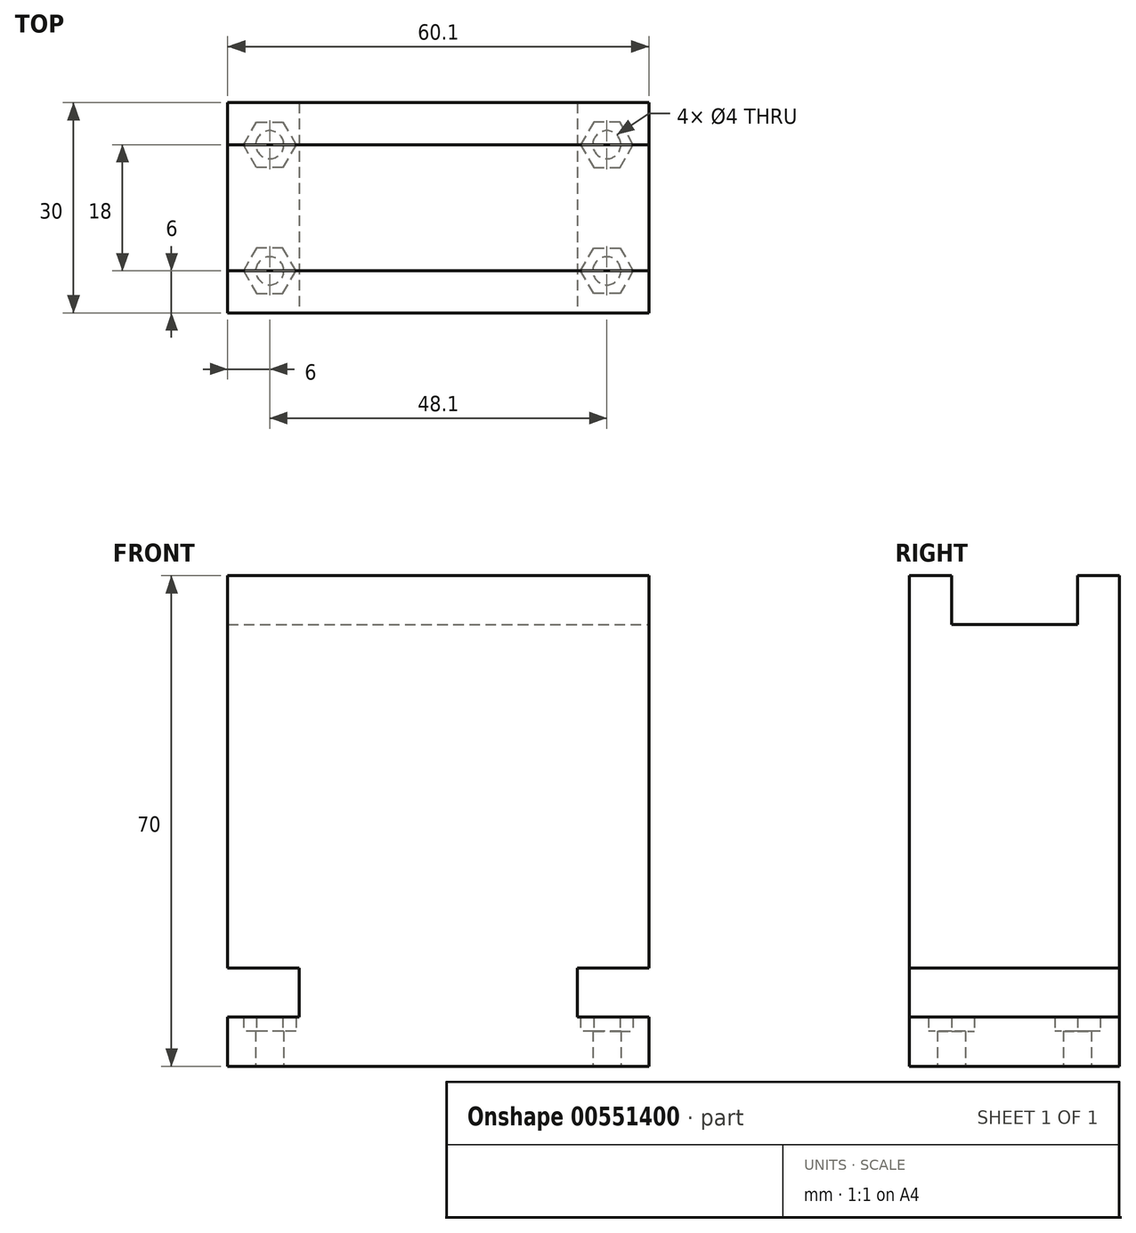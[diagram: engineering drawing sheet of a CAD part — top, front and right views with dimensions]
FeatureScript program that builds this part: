
annotation { "Feature Type Name" : "Feature", "Feature Type Description" : "" }
export const myFeature = defineFeature(function(context is Context, id is Id, definition is map)
    precondition{}
    {
        {
            var Q0;
            Q0=qCreatedBy(makeId("Top.planeOp"),FACE);
            var sketch = newSketch(context, id + "F0", { "sketchPlane" : qUnion([Q0])});
            skLineSegment(sketch, "E0.bottom", {"start": v(-30.05, 15) * mm, "end": v(30.05, 15) * mm});
            skLineSegment(sketch, "E0.top", {"start": v(-30.05, -15) * mm, "end": v(30.05, -15) * mm});
            skLineSegment(sketch, "E0.left", {"start": v(-30.05, 15) * mm, "end": v(-30.05, -15) * mm});
            skLineSegment(sketch, "E0.right", {"start": v(30.05, 15) * mm, "end": v(30.05, -15) * mm});
            skCircle(sketch, "E1", {"center": v(-24.05, 9) * mm, "radius": 2 * mm});
            skCircle(sketch, "E2.MirrorC", {"center": v(24.05, 9) * mm, "radius": 2 * mm});
            skCircle(sketch, "E3.MirrorC", {"center": v(-24.05, -9) * mm, "radius": 2 * mm});
            skCircle(sketch, "E4.MirrorC", {"center": v(24.05, -9) * mm, "radius": 2 * mm});
            skSolve(sketch);
        }
        {
            var Q0;
            Q0 = qSketchRegion(id + "F0", true);
            extrude(context, id + "F1", {"entities" : qUnion([Q0]), "depth" : 5 * mm, "offsetDistance" : 25 * mm});
        }
        {
            var Q0;
            Q0=makeQuery(id+"F1.opExtrude","CAP_FACE",FACE,{"disambiguationData":[OSD([sQuery(id+"F0.wireOp",EDGE,"E0.bottom"),sQuery(id+"F0.wireOp",EDGE,"E0.top"),sQuery(id+"F0.wireOp",EDGE,"E0.left"),sQuery(id+"F0.wireOp",EDGE,"E0.right"),sQuery(id+"F0.wireOp",EDGE,"E1"),sQuery(id+"F0.wireOp",EDGE,"E2.MirrorC"),sQuery(id+"F0.wireOp",EDGE,"E3.MirrorC"),sQuery(id+"F0.wireOp",EDGE,"E4.MirrorC")])],"isStart":false});
            var sketch = newSketch(context, id + "F2", { "sketchPlane" : qUnion([Q0])});
            skCircle(sketch, "E5.cCircle", {"center": v(-24.05, 9) * mm, "radius": 3.25 * mm, "construction": true});
            skLineSegment(sketch, "E5.0", {"start": v(-25.93, 5.75) * mm, "end": v(-27.8, 9) * mm});
            skLineSegment(sketch, "E5.1", {"start": v(-27.8, 9) * mm, "end": v(-25.93, 12.25) * mm});
            skLineSegment(sketch, "E5.2", {"start": v(-25.93, 12.25) * mm, "end": v(-22.17, 12.25) * mm});
            skLineSegment(sketch, "E5.3", {"start": v(-22.17, 12.25) * mm, "end": v(-20.3, 9) * mm});
            skLineSegment(sketch, "E5.4", {"start": v(-20.3, 9) * mm, "end": v(-22.17, 5.75) * mm});
            skLineSegment(sketch, "E5.5", {"start": v(-22.17, 5.75) * mm, "end": v(-25.93, 5.75) * mm});
            skPoint(sketch, "E5.0.midPoint", {"position": v(-26.86, 7.37) * mm});
            skLineSegment(sketch, "E6.MirrorCS", {"start": v(22.17, 5.75) * mm, "end": v(25.93, 5.75) * mm});
            skLineSegment(sketch, "E7.MirrorCS", {"start": v(27.8, 9) * mm, "end": v(25.93, 12.25) * mm});
            skLineSegment(sketch, "E8.MirrorCS", {"start": v(20.3, 9) * mm, "end": v(22.17, 5.75) * mm});
            skLineSegment(sketch, "E9.MirrorCS", {"start": v(22.17, 12.25) * mm, "end": v(20.3, 9) * mm});
            skLineSegment(sketch, "E10.MirrorCS", {"start": v(25.93, 12.25) * mm, "end": v(22.17, 12.25) * mm});
            skLineSegment(sketch, "E11.MirrorCS", {"start": v(25.93, 5.75) * mm, "end": v(27.8, 9) * mm});
            skCircle(sketch, "E12.MirrorC", {"center": v(24.05, 9) * mm, "radius": 3.25 * mm, "construction": true});
            skPoint(sketch, "E13.MirrorP", {"position": v(26.86, 7.37) * mm});
            skLineSegment(sketch, "E14.MirrorCS", {"start": v(22.17, -5.75) * mm, "end": v(25.93, -5.75) * mm});
            skLineSegment(sketch, "E15.MirrorCS", {"start": v(25.93, -5.75) * mm, "end": v(27.8, -9) * mm});
            skLineSegment(sketch, "E16.MirrorCS", {"start": v(27.8, -9) * mm, "end": v(25.93, -12.25) * mm});
            skLineSegment(sketch, "E17.MirrorCS", {"start": v(20.3, -9) * mm, "end": v(22.17, -5.75) * mm});
            skLineSegment(sketch, "E18.MirrorCS", {"start": v(25.93, -12.25) * mm, "end": v(22.17, -12.25) * mm});
            skLineSegment(sketch, "E19.MirrorCS", {"start": v(22.17, -12.25) * mm, "end": v(20.3, -9) * mm});
            skPoint(sketch, "E20.MirrorP", {"position": v(26.86, -7.37) * mm});
            skCircle(sketch, "E21.MirrorC", {"center": v(24.05, -9) * mm, "radius": 3.25 * mm, "construction": true});
            skLineSegment(sketch, "E22.MirrorCS", {"start": v(-22.17, -5.75) * mm, "end": v(-25.93, -5.75) * mm});
            skLineSegment(sketch, "E23.MirrorCS", {"start": v(-20.3, -9) * mm, "end": v(-22.17, -5.75) * mm});
            skLineSegment(sketch, "E24.MirrorCS", {"start": v(-22.17, -12.25) * mm, "end": v(-20.3, -9) * mm});
            skLineSegment(sketch, "E25.MirrorCS", {"start": v(-25.93, -12.25) * mm, "end": v(-22.17, -12.25) * mm});
            skPoint(sketch, "E26.MirrorP", {"position": v(-26.86, -7.37) * mm});
            skLineSegment(sketch, "E27.MirrorCS", {"start": v(-27.8, -9) * mm, "end": v(-25.93, -12.25) * mm});
            skLineSegment(sketch, "E28.MirrorCS", {"start": v(-25.93, -5.75) * mm, "end": v(-27.8, -9) * mm});
            skCircle(sketch, "E29.MirrorC", {"center": v(-24.05, -9) * mm, "radius": 3.25 * mm, "construction": true});
            skSolve(sketch);
        }
        {
            var Q0;
            Q0=makeQuery(id+"F2.imprint","IMPRINT",FACE,{"disambiguationData":[TD([[makeQuery(id+"F2.imprint","IMPRINT",EDGE,{"derivedFrom":sQuery(id+"F2.wireOp",EDGE,"E5.0")}),1.0]])]});
            extrude(context, id + "F3", {"entities" : qUnion([Q0]), "operationType" : NewBodyOperationType.ADD, "depth" : 2 * mm, "offsetDistance" : 25 * mm});
        }
        {
            var Q0;
            Q0=makeQuery(id+"F3.opExtrude","CAP_FACE",FACE,{"disambiguationData":[OSD([sQuery(id+"F0.wireOp",EDGE,"E0.bottom"),sQuery(id+"F0.wireOp",EDGE,"E0.top"),sQuery(id+"F0.wireOp",EDGE,"E0.left"),sQuery(id+"F0.wireOp",EDGE,"E0.right"),sQuery(id+"F2.wireOp",EDGE,"E5.0"),sQuery(id+"F2.wireOp",EDGE,"E5.1"),sQuery(id+"F2.wireOp",EDGE,"E5.2"),sQuery(id+"F2.wireOp",EDGE,"E5.3"),sQuery(id+"F2.wireOp",EDGE,"E5.4"),sQuery(id+"F2.wireOp",EDGE,"E5.5"),sQuery(id+"F2.wireOp",EDGE,"E6.MirrorCS"),sQuery(id+"F2.wireOp",EDGE,"E7.MirrorCS"),sQuery(id+"F2.wireOp",EDGE,"E8.MirrorCS"),sQuery(id+"F2.wireOp",EDGE,"E9.MirrorCS"),sQuery(id+"F2.wireOp",EDGE,"E10.MirrorCS"),sQuery(id+"F2.wireOp",EDGE,"E11.MirrorCS"),sQuery(id+"F2.wireOp",EDGE,"E14.MirrorCS"),sQuery(id+"F2.wireOp",EDGE,"E15.MirrorCS"),sQuery(id+"F2.wireOp",EDGE,"E16.MirrorCS"),sQuery(id+"F2.wireOp",EDGE,"E17.MirrorCS"),sQuery(id+"F2.wireOp",EDGE,"E18.MirrorCS"),sQuery(id+"F2.wireOp",EDGE,"E19.MirrorCS"),sQuery(id+"F2.wireOp",EDGE,"E22.MirrorCS"),sQuery(id+"F2.wireOp",EDGE,"E23.MirrorCS"),sQuery(id+"F2.wireOp",EDGE,"E24.MirrorCS"),sQuery(id+"F2.wireOp",EDGE,"E25.MirrorCS"),sQuery(id+"F2.wireOp",EDGE,"E27.MirrorCS"),sQuery(id+"F2.wireOp",EDGE,"E28.MirrorCS")])],"isStart":false});
            var sketch = newSketch(context, id + "F4", { "sketchPlane" : qUnion([Q0])});
            skLineSegment(sketch, "E30", {"start": v(-19.85, 15) * mm, "end": v(-19.85, -15) * mm});
            skLineSegment(sketch, "E31.MirrorCS", {"start": v(19.85, 15) * mm, "end": v(19.85, -15) * mm});
            skSolve(sketch);
        }
        {
            var Q0;
            {var subQ0=sQuery(id+"F4.wireOp",EDGE,"E30");Q0=makeQuery(id+"F4.imprint","IMPRINT",FACE,{"disambiguationData":[TD([[makeQuery(id+"F4.imprint","IMPRINT",EDGE,{"derivedFrom":subQ0}),1.0]])]});}
            extrude(context, id + "F5", {"entities" : qUnion([Q0]), "operationType" : NewBodyOperationType.ADD, "depth" : 7 * mm, "offsetDistance" : 25 * mm});
        }
        {
            var Q0;
            Q0=makeQuery(id+"F5.opExtrude","CAP_FACE",FACE,{"disambiguationData":[OSD([sQuery(id+"F0.wireOp",EDGE,"E0.bottom"),sQuery(id+"F0.wireOp",EDGE,"E0.top"),sQuery(id+"F4.wireOp",EDGE,"E30"),sQuery(id+"F4.wireOp",EDGE,"E31.MirrorCS")])],"isStart":false});
            var sketch = newSketch(context, id + "F6", { "sketchPlane" : qUnion([Q0])});
            skLineSegment(sketch, "E32.bottom", {"start": v(-30.05, 15) * mm, "end": v(30.05, 15) * mm});
            skLineSegment(sketch, "E32.top", {"start": v(-30.05, -15) * mm, "end": v(30.05, -15) * mm});
            skLineSegment(sketch, "E32.left", {"start": v(-30.05, 15) * mm, "end": v(-30.05, -15) * mm});
            skLineSegment(sketch, "E32.right", {"start": v(30.05, 15) * mm, "end": v(30.05, -15) * mm});
            skSolve(sketch);
        }
        {
            var Q0;
            Q0 = qSketchRegion(id + "F6", true);
            extrude(context, id + "F7", {"entities" : qUnion([Q0]), "operationType" : NewBodyOperationType.ADD, "depth" : 49 * mm, "offsetDistance" : 25 * mm});
        }
        {
            var Q0;
            Q0=makeQuery(id+"F7.opExtrude","CAP_FACE",FACE,{"disambiguationData":[OSD([sQuery(id+"F6.wireOp",EDGE,"E32.bottom"),sQuery(id+"F6.wireOp",EDGE,"E32.top"),sQuery(id+"F6.wireOp",EDGE,"E32.left"),sQuery(id+"F6.wireOp",EDGE,"E32.right")])],"isStart":false});
            var sketch = newSketch(context, id + "F8", { "sketchPlane" : qUnion([Q0])});
            skLineSegment(sketch, "E33", {"start": v(-30.05, 9) * mm, "end": v(30.05, 9) * mm});
            skLineSegment(sketch, "E34.MirrorCS", {"start": v(-30.05, -9) * mm, "end": v(30.05, -9) * mm});
            skSolve(sketch);
        }
        {
            var Q0;
            Q0 = qSketchRegion(id + "F8", true);
            var Q1;
            {var subQ0=sQuery(id+"F8.wireOp",EDGE,"E33");Q1=makeQuery(id+"F8.imprint","IMPRINT",FACE,{"disambiguationData":[TD([[makeQuery(id+"F8.imprint","IMPRINT",EDGE,{"derivedFrom":subQ0}),1.0]])]});}
            var Q2;
            {var subQ0=sQuery(id+"F8.wireOp",EDGE,"E34.MirrorCS");Q2=makeQuery(id+"F8.imprint","IMPRINT",FACE,{"disambiguationData":[TD([[makeQuery(id+"F8.imprint","IMPRINT",EDGE,{"derivedFrom":subQ0}),-1.0]])]});}
            extrude(context, id + "F9", {"entities" : qUnion([Q0, Q1, Q2]), "operationType" : NewBodyOperationType.ADD, "depth" : 7 * mm, "offsetDistance" : 25 * mm});
        }
    });
